# Revit family: Towel_Bar-American_Standard-Delancey-70520XX_Series
name_source: partatom
category: Specialty Equipment
units: mm (PartAtom-declared; Revit-internal decimal feet)

## family parameters
Cut with Voids When Loaded = No
Host = Face
OmniClass Number = 23.40.20.21.27
OmniClass Title = Towel Bars
Part Type = Normal
Room Calculation Point = No
Round Connector Dimension = Use Diameter
Shared = Yes

## types (10) — shared parameters
Default Elevation = 44"
Description = Delancey Towel Bar
Height = 2 3/16"
Installation Instruction Link = https://lixil.cdn.celum.cloud
Installation Type = Wall Mounted
Length = 3 7/8"
Manufacturer = American Standard
Price = Prices may vary. Please consult Manufacturer Representative for most up-to-date price list.
Product Documentation Link = https://lixil.cdn.celum.cloud
Product Page URL = https://www.americanstandard-us.com
Revised Date = 02/25/2024
URL = http://www.americanstandard-us.com
Warranty Information = Lifetime Warranty

## per-type parameters (varying)
| type | Assembly Code | Finish | Material | Width |
| 7052018.002 | C1030200 | Metal-American Standard-002-Polished Chrome | Metal-American Standard-002-Polished Chrome | 18" |
| 7052018.295 | C1030220 | Metal-American Standard-295-Brushed Nickel | Metal-American Standard-295-Brushed Nickel | 18" |
| 7052018.013 | C1030220 | Metal-American Standard-013-Polished Nickel | Metal-American Standard-013-Polished Nickel | 18" |
| 7052018.278 | C1030220 | Metal-American Standard-278-Legacy Bronze | Metal-American Standard-278-Legacy Bronze | 18" |
| 7052024.002 | C1030220 | Metal-American Standard-002-Polished Chrome | Metal-American Standard-002-Polished Chrome | 24" |
| 7052024.295 | C1030220 | Metal-American Standard-295-Brushed Nickel | Metal-American Standard-295-Brushed Nickel | 24" |
| 7052024.013 | C1030220 | Metal-American Standard-013-Polished Nickel | Metal-American Standard-013-Polished Nickel | 24" |
| 7052024.278 | C1030220 | Metal-American Standard-278-Legacy Bronze | Metal-American Standard-278-Legacy Bronze | 24" |
| 7052018.GN0 | C1030220 | Metal-American Standard-GN0-Brushed Cool Sunrise | Metal-American Standard-GN0-Brushed Cool Sunrise | 18" |
| 7052024.GN0 | C1030220 | Metal-American Standard-GN0-Brushed Cool Sunrise | Metal-American Standard-GN0-Brushed Cool Sunrise | 24" |

note: column(s) folded — value = type name in every type: Model

## geometry (parser evidence)
native form markers: Sweep x3
no freeform markers — native parametric forms only
